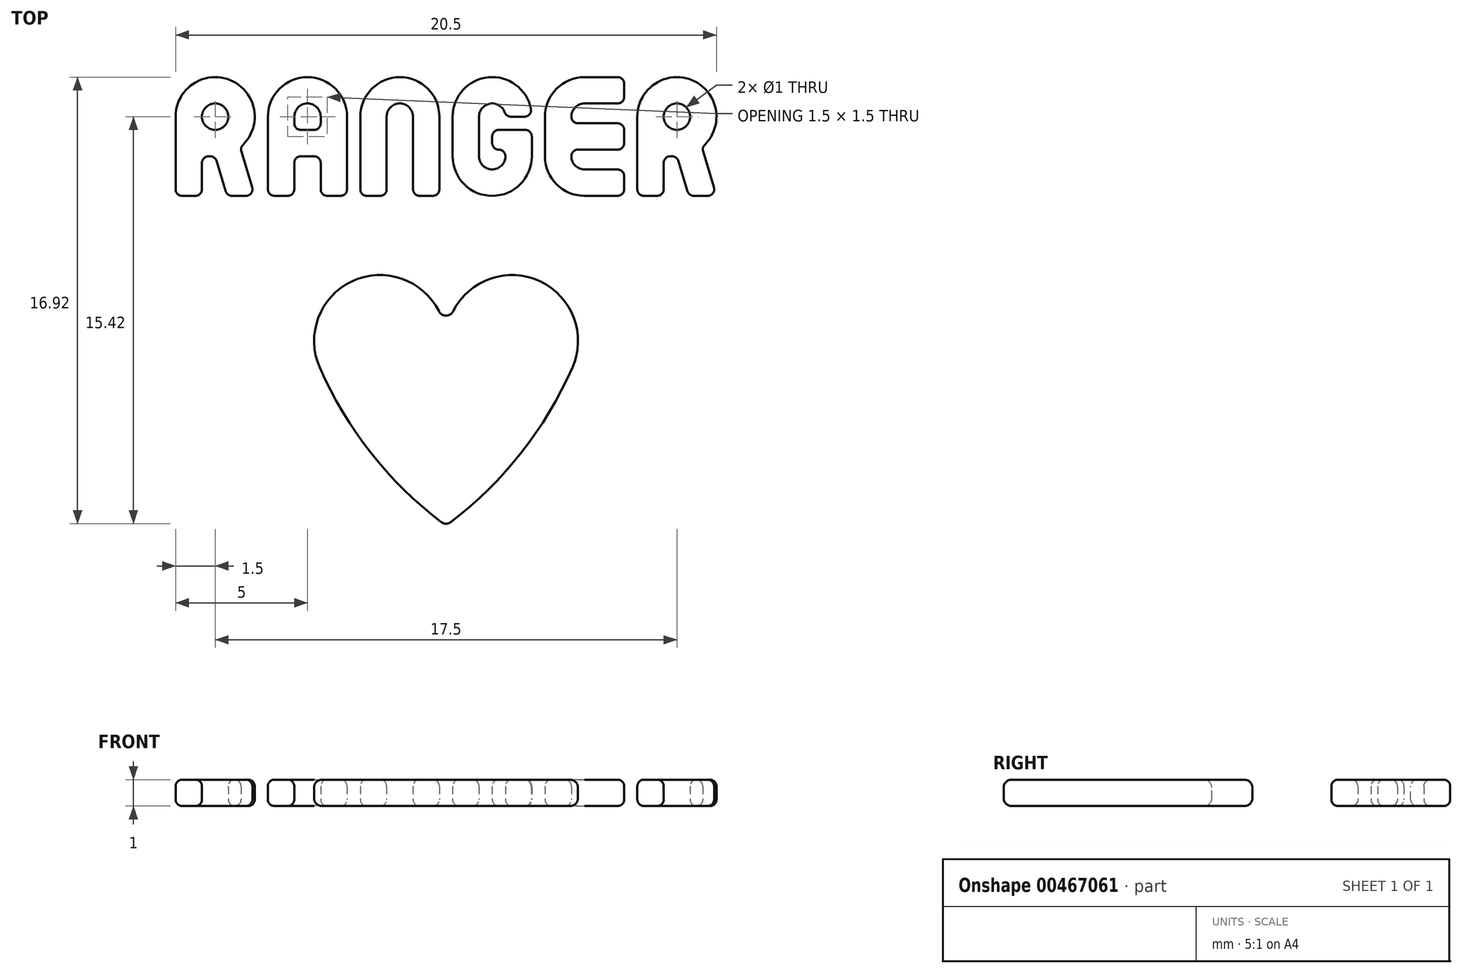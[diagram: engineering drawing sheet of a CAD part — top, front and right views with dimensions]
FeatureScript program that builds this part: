
annotation { "Feature Type Name" : "Feature", "Feature Type Description" : "" }
export const myFeature = defineFeature(function(context is Context, id is Id, definition is map)
    precondition{}
    {
        {
            var Q0;
            Q0=qCreatedBy(makeId("Top.planeOp"),FACE);
            var sketch = newSketch(context, id + "F0", { "sketchPlane" : qUnion([Q0])});
            skArc(sketch, "E0", {"start": v(-15, 3) * mm, "mid": v(-13.5, 4.5) * mm, "end": v(-12, 3) * mm});
            skLineSegment(sketch, "E1", {"start": v(-15, 3) * mm, "end": v(-15, 0) * mm});
            skLineSegment(sketch, "E2", {"start": v(-12, 3) * mm, "end": v(-12, 0) * mm});
            skLineSegment(sketch, "E3.0", {"start": v(-13, 3) * mm, "end": v(-13, 2.5) * mm});
            skArc(sketch, "E3.1", {"start": v(-14, 3) * mm, "mid": v(-13.5, 3.5) * mm, "end": v(-13, 3) * mm});
            skLineSegment(sketch, "E3.2", {"start": v(-14, 3) * mm, "end": v(-14, 2.5) * mm});
            skLineSegment(sketch, "E4.bottom", {"start": v(-14, 2.5) * mm, "end": v(-13, 2.5) * mm});
            skLineSegment(sketch, "E4.top", {"start": v(-14, 1.5) * mm, "end": v(-13, 1.5) * mm});
            skLineSegment(sketch, "E5.trimOffspring", {"start": v(-13, 1.5) * mm, "end": v(-13, 0) * mm});
            skLineSegment(sketch, "E6.trimOffspring", {"start": v(-14, 1.5) * mm, "end": v(-14, 0) * mm});
            skLineSegment(sketch, "E7", {"start": v(-15, 0) * mm, "end": v(-14, 0) * mm});
            skLineSegment(sketch, "E8.trimOffspring", {"start": v(-13, 0) * mm, "end": v(-12, 0) * mm});
            skLineSegment(sketch, "E9", {"start": v(-16.02, 4.5) * mm, "end": v(-10.39, 4.5) * mm, "construction": true});
            skArc(sketch, "E10", {"start": v(-11.5, 3) * mm, "mid": v(-10, 4.5) * mm, "end": v(-8.5, 3) * mm});
            skLineSegment(sketch, "E11", {"start": v(-11.5, 3) * mm, "end": v(-11.5, 0) * mm});
            skLineSegment(sketch, "E12", {"start": v(-8.5, 3) * mm, "end": v(-8.5, 0) * mm});
            skArc(sketch, "E13.1", {"start": v(-10.5, 3) * mm, "mid": v(-10, 3.5) * mm, "end": v(-9.5, 3) * mm});
            skLineSegment(sketch, "E13.2", {"start": v(-10.5, 3) * mm, "end": v(-10.5, 0) * mm});
            skLineSegment(sketch, "E14", {"start": v(-11.5, 0) * mm, "end": v(-10.5, 0) * mm});
            skLineSegment(sketch, "E15.trimOffspring", {"start": v(-9.5, 0) * mm, "end": v(-8.5, 0) * mm});
            skLineSegment(sketch, "E16", {"start": v(-9.5, 3) * mm, "end": v(-9.5, 0) * mm});
            skArc(sketch, "E17.0.startCap", {"start": v(-7, 3) * mm, "mid": v(-6.5, 3.5) * mm, "end": v(-6, 3) * mm});
            skArc(sketch, "E17.0.endCap", {"start": v(-6, 1.5) * mm, "mid": v(-6.5, 1) * mm, "end": v(-7, 1.5) * mm});
            skLineSegment(sketch, "E17.0.right", {"start": v(-7, 3) * mm, "end": v(-7, 1.5) * mm});
            skArc(sketch, "E18.0.startCap", {"start": v(-8, 3) * mm, "mid": v(-6.5, 4.5) * mm, "end": v(-5, 3) * mm});
            skArc(sketch, "E18.0.endCap", {"start": v(-5, 1.5) * mm, "mid": v(-6.5, 0) * mm, "end": v(-8, 1.5) * mm});
            skLineSegment(sketch, "E18.0.right", {"start": v(-8, 3) * mm, "end": v(-8, 1.5) * mm});
            skLineSegment(sketch, "E19.trimOffspring", {"start": v(-6, 1.75) * mm, "end": v(-6, 1.5) * mm});
            skLineSegment(sketch, "E20", {"start": v(-5, 1.5) * mm, "end": v(-5, 2.5) * mm});
            skLineSegment(sketch, "E21", {"start": v(-5, 2.5) * mm, "end": v(-6.5, 2.5) * mm});
            skLineSegment(sketch, "E22", {"start": v(-6.5, 2.5) * mm, "end": v(-6.5, 1.75) * mm});
            skLineSegment(sketch, "E23", {"start": v(-6.5, 1.75) * mm, "end": v(-6, 1.75) * mm});
            skLineSegment(sketch, "E24", {"start": v(-6, 3) * mm, "end": v(-5, 3) * mm});
            skArc(sketch, "E25", {"start": v(-4.5, 3) * mm, "mid": v(-4.06, 4.06) * mm, "end": v(-3, 4.5) * mm});
            skLineSegment(sketch, "E26", {"start": v(-3, 4.5) * mm, "end": v(-1.5, 4.5) * mm});
            skLineSegment(sketch, "E27", {"start": v(-1.5, 4.5) * mm, "end": v(-1.5, 3.5) * mm});
            skLineSegment(sketch, "E28", {"start": v(-1.5, 3.5) * mm, "end": v(-3, 3.5) * mm});
            skArc(sketch, "E29", {"start": v(-3, 3.5) * mm, "mid": v(-3.35, 3.35) * mm, "end": v(-3.5, 3) * mm});
            skLineSegment(sketch, "E30", {"start": v(-4.5, 3) * mm, "end": v(-4.5, 1.5) * mm});
            skLineSegment(sketch, "E31", {"start": v(-3.5, 3) * mm, "end": v(-3.5, 2.75) * mm});
            skArc(sketch, "E32", {"start": v(-3.5, 1.5) * mm, "mid": v(-3.35, 1.15) * mm, "end": v(-3, 1) * mm});
            skArc(sketch, "E33", {"start": v(-4.5, 1.5) * mm, "mid": v(-4.06, 0.44) * mm, "end": v(-3, 0) * mm});
            skLineSegment(sketch, "E34", {"start": v(-3, 1) * mm, "end": v(-1.5, 1) * mm});
            skLineSegment(sketch, "E35", {"start": v(-1.5, 1) * mm, "end": v(-1.5, 0) * mm});
            skLineSegment(sketch, "E36", {"start": v(-1.5, 0) * mm, "end": v(-3, 0) * mm});
            skLineSegment(sketch, "E37.bottom", {"start": v(-3.5, 2.75) * mm, "end": v(-1.5, 2.75) * mm});
            skLineSegment(sketch, "E37.top", {"start": v(-3.5, 1.75) * mm, "end": v(-1.5, 1.75) * mm});
            skLineSegment(sketch, "E37.right", {"start": v(-1.5, 2.75) * mm, "end": v(-1.5, 1.75) * mm});
            skLineSegment(sketch, "E38.trimOffspring", {"start": v(-3.5, 1.75) * mm, "end": v(-3.5, 1.5) * mm});
            skLineSegment(sketch, "E39", {"start": v(-1.5, 2.25) * mm, "end": v(-3.17, 2.25) * mm, "construction": true});
            skPoint(sketch, "E39.endSnap0", {"position": v(-1.5, 2.25) * mm});
            skLineSegment(sketch, "E40", {"start": v(-1, 0) * mm, "end": v(-1, 3) * mm});
            skLineSegment(sketch, "E41", {"start": v(0, 1.5) * mm, "end": v(0, 0) * mm});
            skLineSegment(sketch, "E42", {"start": v(0, 0) * mm, "end": v(-1, 0) * mm});
            skPoint(sketch, "E43.orphan", {"position": v(0, 2.75) * mm});
            skCircle(sketch, "E44", {"center": v(0.5, 3) * mm, "radius": 0.5 * mm});
            skLineSegment(sketch, "E45", {"start": v(0.5, 1.5) * mm, "end": v(0, 1.5) * mm});
            skLineSegment(sketch, "E46", {"start": v(0.5, 1.5) * mm, "end": v(0.96, 0) * mm});
            skLineSegment(sketch, "E47", {"start": v(0.96, 0) * mm, "end": v(2, 0) * mm});
            skLineSegment(sketch, "E48", {"start": v(2, 0) * mm, "end": v(1.44, 1.83) * mm});
            skArc(sketch, "E49.trimOffspring", {"start": v(1.44, 1.83) * mm, "mid": v(1.15, 4.35) * mm, "end": v(-1, 3) * mm});
            skLineSegment(sketch, "E50", {"start": v(2, 3.78) * mm, "end": v(2, 0) * mm, "construction": true});
            skLineSegment(sketch, "E51", {"start": v(0.5, 3) * mm, "end": v(0.5, 0.89) * mm, "construction": true});
            skLineSegment(sketch, "E52", {"start": v(-18.5, 0) * mm, "end": v(-18.5, 3) * mm});
            skLineSegment(sketch, "E53", {"start": v(-17.5, 1.5) * mm, "end": v(-17.5, 0) * mm});
            skLineSegment(sketch, "E54", {"start": v(-17.5, 0) * mm, "end": v(-18.5, 0) * mm});
            skCircle(sketch, "E55", {"center": v(-17, 3) * mm, "radius": 0.5 * mm});
            skLineSegment(sketch, "E56", {"start": v(-17, 1.5) * mm, "end": v(-17.5, 1.5) * mm});
            skLineSegment(sketch, "E57", {"start": v(-17, 1.5) * mm, "end": v(-16.54, 0) * mm});
            skLineSegment(sketch, "E58", {"start": v(-16.54, 0) * mm, "end": v(-15.5, 0) * mm});
            skLineSegment(sketch, "E59", {"start": v(-15.5, 0) * mm, "end": v(-16.06, 1.83) * mm});
            skArc(sketch, "E60.trimOffspring", {"start": v(-16.06, 1.83) * mm, "mid": v(-16.35, 4.35) * mm, "end": v(-18.5, 3) * mm});
            skLineSegment(sketch, "E61", {"start": v(-15.5, 5.59) * mm, "end": v(-15.5, 1.81) * mm, "construction": true});
            skLineSegment(sketch, "E62", {"start": v(-17, 3) * mm, "end": v(-17, 2.7) * mm, "construction": true});
            skSolve(sketch);
        }
        {
            var Q0;
            Q0 = qSketchRegion(id + "F0", true);
            extrude(context, id + "F1", {"entities" : qUnion([Q0]), "depth" : 1 * mm});
        }
        {
            var Q0;
            Q0=makeQuery(id+"F1.opExtrude","CAP_FACE",FACE,{"disambiguationData":[OSD([sQuery(id+"F0.wireOp",EDGE,"E52"),sQuery(id+"F0.wireOp",EDGE,"E53"),sQuery(id+"F0.wireOp",EDGE,"E54"),sQuery(id+"F0.wireOp",EDGE,"E55"),sQuery(id+"F0.wireOp",EDGE,"E56"),sQuery(id+"F0.wireOp",EDGE,"E57"),sQuery(id+"F0.wireOp",EDGE,"E58"),sQuery(id+"F0.wireOp",EDGE,"E59"),sQuery(id+"F0.wireOp",EDGE,"E60.trimOffspring")])],"isStart":false});
            var Q1;
            Q1=makeQuery(id+"F1.opExtrude","CAP_FACE",FACE,{"disambiguationData":[OSD([sQuery(id+"F0.wireOp",EDGE,"E0"),sQuery(id+"F0.wireOp",EDGE,"E1"),sQuery(id+"F0.wireOp",EDGE,"E2"),sQuery(id+"F0.wireOp",EDGE,"E3.0"),sQuery(id+"F0.wireOp",EDGE,"E3.1"),sQuery(id+"F0.wireOp",EDGE,"E3.2"),sQuery(id+"F0.wireOp",EDGE,"E4.bottom"),sQuery(id+"F0.wireOp",EDGE,"E4.top"),sQuery(id+"F0.wireOp",EDGE,"E5.trimOffspring"),sQuery(id+"F0.wireOp",EDGE,"E6.trimOffspring"),sQuery(id+"F0.wireOp",EDGE,"E7"),sQuery(id+"F0.wireOp",EDGE,"E8.trimOffspring")])],"isStart":false});
            var Q2;
            Q2=makeQuery(id+"F1.opExtrude","CAP_FACE",FACE,{"disambiguationData":[OSD([sQuery(id+"F0.wireOp",EDGE,"E10"),sQuery(id+"F0.wireOp",EDGE,"E11"),sQuery(id+"F0.wireOp",EDGE,"E12"),sQuery(id+"F0.wireOp",EDGE,"E13.1"),sQuery(id+"F0.wireOp",EDGE,"E13.2"),sQuery(id+"F0.wireOp",EDGE,"E14"),sQuery(id+"F0.wireOp",EDGE,"E15.trimOffspring"),sQuery(id+"F0.wireOp",EDGE,"E16")])],"isStart":false});
            var Q3;
            Q3=makeQuery(id+"F1.opExtrude","CAP_FACE",FACE,{"disambiguationData":[OSD([sQuery(id+"F0.wireOp",EDGE,"E17.0.startCap"),sQuery(id+"F0.wireOp",EDGE,"E17.0.endCap"),sQuery(id+"F0.wireOp",EDGE,"E17.0.right"),sQuery(id+"F0.wireOp",EDGE,"E18.0.startCap"),sQuery(id+"F0.wireOp",EDGE,"E18.0.endCap"),sQuery(id+"F0.wireOp",EDGE,"E18.0.right"),sQuery(id+"F0.wireOp",EDGE,"E19.trimOffspring"),sQuery(id+"F0.wireOp",EDGE,"E20"),sQuery(id+"F0.wireOp",EDGE,"E21"),sQuery(id+"F0.wireOp",EDGE,"E22"),sQuery(id+"F0.wireOp",EDGE,"E23"),sQuery(id+"F0.wireOp",EDGE,"E24")])],"isStart":false});
            var Q4;
            Q4=makeQuery(id+"F1.opExtrude","CAP_FACE",FACE,{"disambiguationData":[OSD([sQuery(id+"F0.wireOp",EDGE,"E25"),sQuery(id+"F0.wireOp",EDGE,"E26"),sQuery(id+"F0.wireOp",EDGE,"E27"),sQuery(id+"F0.wireOp",EDGE,"E28"),sQuery(id+"F0.wireOp",EDGE,"E29"),sQuery(id+"F0.wireOp",EDGE,"E30"),sQuery(id+"F0.wireOp",EDGE,"E31"),sQuery(id+"F0.wireOp",EDGE,"E32"),sQuery(id+"F0.wireOp",EDGE,"E33"),sQuery(id+"F0.wireOp",EDGE,"E34"),sQuery(id+"F0.wireOp",EDGE,"E35"),sQuery(id+"F0.wireOp",EDGE,"E36"),sQuery(id+"F0.wireOp",EDGE,"E37.bottom"),sQuery(id+"F0.wireOp",EDGE,"E37.top"),sQuery(id+"F0.wireOp",EDGE,"E37.right"),sQuery(id+"F0.wireOp",EDGE,"E38.trimOffspring")])],"isStart":false});
            var Q5;
            Q5=makeQuery(id+"F1.opExtrude","CAP_FACE",FACE,{"disambiguationData":[OSD([sQuery(id+"F0.wireOp",EDGE,"E40"),sQuery(id+"F0.wireOp",EDGE,"E41"),sQuery(id+"F0.wireOp",EDGE,"E42"),sQuery(id+"F0.wireOp",EDGE,"E44"),sQuery(id+"F0.wireOp",EDGE,"E45"),sQuery(id+"F0.wireOp",EDGE,"E46"),sQuery(id+"F0.wireOp",EDGE,"E47"),sQuery(id+"F0.wireOp",EDGE,"E48"),sQuery(id+"F0.wireOp",EDGE,"E49.trimOffspring")])],"isStart":false});
            var Q6;
            Q6=makeQuery(id+"F1.opExtrude","CAP_FACE",FACE,{"disambiguationData":[OSD([sQuery(id+"F0.wireOp",EDGE,"E40"),sQuery(id+"F0.wireOp",EDGE,"E41"),sQuery(id+"F0.wireOp",EDGE,"E42"),sQuery(id+"F0.wireOp",EDGE,"E44"),sQuery(id+"F0.wireOp",EDGE,"E45"),sQuery(id+"F0.wireOp",EDGE,"E46"),sQuery(id+"F0.wireOp",EDGE,"E47"),sQuery(id+"F0.wireOp",EDGE,"E48"),sQuery(id+"F0.wireOp",EDGE,"E49.trimOffspring")])],"isStart":true});
            var Q7;
            Q7=makeQuery(id+"F1.opExtrude","CAP_FACE",FACE,{"disambiguationData":[OSD([sQuery(id+"F0.wireOp",EDGE,"E25"),sQuery(id+"F0.wireOp",EDGE,"E26"),sQuery(id+"F0.wireOp",EDGE,"E27"),sQuery(id+"F0.wireOp",EDGE,"E28"),sQuery(id+"F0.wireOp",EDGE,"E29"),sQuery(id+"F0.wireOp",EDGE,"E30"),sQuery(id+"F0.wireOp",EDGE,"E31"),sQuery(id+"F0.wireOp",EDGE,"E32"),sQuery(id+"F0.wireOp",EDGE,"E33"),sQuery(id+"F0.wireOp",EDGE,"E34"),sQuery(id+"F0.wireOp",EDGE,"E35"),sQuery(id+"F0.wireOp",EDGE,"E36"),sQuery(id+"F0.wireOp",EDGE,"E37.bottom"),sQuery(id+"F0.wireOp",EDGE,"E37.top"),sQuery(id+"F0.wireOp",EDGE,"E37.right"),sQuery(id+"F0.wireOp",EDGE,"E38.trimOffspring")])],"isStart":true});
            var Q8;
            Q8=makeQuery(id+"F1.opExtrude","CAP_FACE",FACE,{"disambiguationData":[OSD([sQuery(id+"F0.wireOp",EDGE,"E17.0.startCap"),sQuery(id+"F0.wireOp",EDGE,"E17.0.endCap"),sQuery(id+"F0.wireOp",EDGE,"E17.0.right"),sQuery(id+"F0.wireOp",EDGE,"E18.0.startCap"),sQuery(id+"F0.wireOp",EDGE,"E18.0.endCap"),sQuery(id+"F0.wireOp",EDGE,"E18.0.right"),sQuery(id+"F0.wireOp",EDGE,"E19.trimOffspring"),sQuery(id+"F0.wireOp",EDGE,"E20"),sQuery(id+"F0.wireOp",EDGE,"E21"),sQuery(id+"F0.wireOp",EDGE,"E22"),sQuery(id+"F0.wireOp",EDGE,"E23"),sQuery(id+"F0.wireOp",EDGE,"E24")])],"isStart":true});
            var Q9;
            Q9=makeQuery(id+"F1.opExtrude","CAP_FACE",FACE,{"disambiguationData":[OSD([sQuery(id+"F0.wireOp",EDGE,"E10"),sQuery(id+"F0.wireOp",EDGE,"E11"),sQuery(id+"F0.wireOp",EDGE,"E12"),sQuery(id+"F0.wireOp",EDGE,"E13.1"),sQuery(id+"F0.wireOp",EDGE,"E13.2"),sQuery(id+"F0.wireOp",EDGE,"E14"),sQuery(id+"F0.wireOp",EDGE,"E15.trimOffspring"),sQuery(id+"F0.wireOp",EDGE,"E16")])],"isStart":true});
            var Q10;
            Q10=makeQuery(id+"F1.opExtrude","CAP_FACE",FACE,{"disambiguationData":[OSD([sQuery(id+"F0.wireOp",EDGE,"E0"),sQuery(id+"F0.wireOp",EDGE,"E1"),sQuery(id+"F0.wireOp",EDGE,"E2"),sQuery(id+"F0.wireOp",EDGE,"E3.0"),sQuery(id+"F0.wireOp",EDGE,"E3.1"),sQuery(id+"F0.wireOp",EDGE,"E3.2"),sQuery(id+"F0.wireOp",EDGE,"E4.bottom"),sQuery(id+"F0.wireOp",EDGE,"E4.top"),sQuery(id+"F0.wireOp",EDGE,"E5.trimOffspring"),sQuery(id+"F0.wireOp",EDGE,"E6.trimOffspring"),sQuery(id+"F0.wireOp",EDGE,"E7"),sQuery(id+"F0.wireOp",EDGE,"E8.trimOffspring")])],"isStart":true});
            var Q11;
            Q11=makeQuery(id+"F1.opExtrude","CAP_FACE",FACE,{"disambiguationData":[OSD([sQuery(id+"F0.wireOp",EDGE,"E52"),sQuery(id+"F0.wireOp",EDGE,"E53"),sQuery(id+"F0.wireOp",EDGE,"E54"),sQuery(id+"F0.wireOp",EDGE,"E55"),sQuery(id+"F0.wireOp",EDGE,"E56"),sQuery(id+"F0.wireOp",EDGE,"E57"),sQuery(id+"F0.wireOp",EDGE,"E58"),sQuery(id+"F0.wireOp",EDGE,"E59"),sQuery(id+"F0.wireOp",EDGE,"E60.trimOffspring")])],"isStart":true});
            var Q12;
            Q12=makeQuery(id+"F1.opExtrude","SWEPT_FACE",FACE,{"disambiguationData":[OSD([sQuery(id+"F0.wireOp",EDGE,"E21")])]});
            var Q13;
            Q13=makeQuery(id+"F1.opExtrude","SWEPT_FACE",FACE,{"disambiguationData":[OSD([sQuery(id+"F0.wireOp",EDGE,"E17.0.endCap")])]});
            var Q14;
            Q14=makeQuery(id+"F1.opExtrude","SWEPT_FACE",FACE,{"disambiguationData":[OSD([sQuery(id+"F0.wireOp",EDGE,"E18.0.endCap")])]});
            var Q15;
            Q15=makeQuery(id+"F1.opExtrude","SWEPT_FACE",FACE,{"disambiguationData":[OSD([sQuery(id+"F0.wireOp",EDGE,"E36")])]});
            var Q16;
            Q16=makeQuery(id+"F1.opExtrude","SWEPT_FACE",FACE,{"disambiguationData":[OSD([sQuery(id+"F0.wireOp",EDGE,"E35")])]});
            var Q17;
            Q17=makeQuery(id+"F1.opExtrude","SWEPT_FACE",FACE,{"disambiguationData":[OSD([sQuery(id+"F0.wireOp",EDGE,"E37.top")])]});
            var Q18;
            Q18=makeQuery(id+"F1.opExtrude","SWEPT_FACE",FACE,{"disambiguationData":[OSD([sQuery(id+"F0.wireOp",EDGE,"E34")])]});
            var Q19;
            Q19=makeQuery(id+"F1.opExtrude","SWEPT_FACE",FACE,{"disambiguationData":[OSD([sQuery(id+"F0.wireOp",EDGE,"E37.bottom")])]});
            var Q20;
            Q20=makeQuery(id+"F1.opExtrude","SWEPT_FACE",FACE,{"disambiguationData":[OSD([sQuery(id+"F0.wireOp",EDGE,"E28")])]});
            var Q21;
            Q21=makeQuery(id+"F1.opExtrude","SWEPT_FACE",FACE,{"disambiguationData":[OSD([sQuery(id+"F0.wireOp",EDGE,"E26")])]});
            var Q22;
            Q22=makeQuery(id+"F1.opExtrude","SWEPT_FACE",FACE,{"disambiguationData":[OSD([sQuery(id+"F0.wireOp",EDGE,"E47")])]});
            var Q23;
            Q23=makeQuery(id+"F1.opExtrude","SWEPT_FACE",FACE,{"disambiguationData":[OSD([sQuery(id+"F0.wireOp",EDGE,"E42")])]});
            var Q24;
            Q24=makeQuery(id+"F1.opExtrude","SWEPT_FACE",FACE,{"disambiguationData":[OSD([sQuery(id+"F0.wireOp",EDGE,"E45")])]});
            var Q25;
            Q25=makeQuery(id+"F1.opExtrude","SWEPT_FACE",FACE,{"disambiguationData":[OSD([sQuery(id+"F0.wireOp",EDGE,"E41")])]});
            var Q26;
            Q26=makeQuery(id+"F1.opExtrude","SWEPT_FACE",FACE,{"disambiguationData":[OSD([sQuery(id+"F0.wireOp",EDGE,"E46")])]});
            var Q27;
            Q27=makeQuery(id+"F1.opExtrude","SWEPT_FACE",FACE,{"disambiguationData":[OSD([sQuery(id+"F0.wireOp",EDGE,"E49.trimOffspring")])]});
            var Q28;
            Q28=makeQuery(id+"F1.opExtrude","SWEPT_FACE",FACE,{"disambiguationData":[OSD([sQuery(id+"F0.wireOp",EDGE,"E23")])]});
            var Q29;
            Q29=makeQuery(id+"F1.opExtrude","SWEPT_FACE",FACE,{"disambiguationData":[OSD([sQuery(id+"F0.wireOp",EDGE,"E24")])]});
            var Q30;
            Q30=makeQuery(id+"F1.opExtrude","SWEPT_FACE",FACE,{"disambiguationData":[OSD([sQuery(id+"F0.wireOp",EDGE,"E17.0.startCap")])]});
            var Q31;
            Q31=makeQuery(id+"F1.opExtrude","SWEPT_FACE",FACE,{"disambiguationData":[OSD([sQuery(id+"F0.wireOp",EDGE,"E15.trimOffspring")])]});
            var Q32;
            Q32=makeQuery(id+"F1.opExtrude","SWEPT_FACE",FACE,{"disambiguationData":[OSD([sQuery(id+"F0.wireOp",EDGE,"E14")])]});
            var Q33;
            Q33=makeQuery(id+"F1.opExtrude","SWEPT_FACE",FACE,{"disambiguationData":[OSD([sQuery(id+"F0.wireOp",EDGE,"E8.trimOffspring")])]});
            var Q34;
            Q34=makeQuery(id+"F1.opExtrude","SWEPT_FACE",FACE,{"disambiguationData":[OSD([sQuery(id+"F0.wireOp",EDGE,"E4.bottom")])]});
            var Q35;
            Q35=makeQuery(id+"F1.opExtrude","SWEPT_FACE",FACE,{"disambiguationData":[OSD([sQuery(id+"F0.wireOp",EDGE,"E4.top")])]});
            var Q36;
            Q36=makeQuery(id+"F1.opExtrude","SWEPT_FACE",FACE,{"disambiguationData":[OSD([sQuery(id+"F0.wireOp",EDGE,"E7")])]});
            var Q37;
            Q37=makeQuery(id+"F1.opExtrude","SWEPT_FACE",FACE,{"disambiguationData":[OSD([sQuery(id+"F0.wireOp",EDGE,"E58")])]});
            var Q38;
            Q38=makeQuery(id+"F1.opExtrude","SWEPT_FACE",FACE,{"disambiguationData":[OSD([sQuery(id+"F0.wireOp",EDGE,"E54")])]});
            var Q39;
            Q39=makeQuery(id+"F1.opExtrude","SWEPT_FACE",FACE,{"disambiguationData":[OSD([sQuery(id+"F0.wireOp",EDGE,"E56")])]});
            var Q40;
            Q40=makeQuery(id+"F1.opExtrude","SWEPT_FACE",FACE,{"disambiguationData":[OSD([sQuery(id+"F0.wireOp",EDGE,"E53")])]});
            var Q41;
            Q41=makeQuery(id+"F1.opExtrude","SWEPT_FACE",FACE,{"disambiguationData":[OSD([sQuery(id+"F0.wireOp",EDGE,"E57")])]});
            var Q42;
            Q42=makeQuery(id+"F1.opExtrude","SWEPT_FACE",FACE,{"disambiguationData":[OSD([sQuery(id+"F0.wireOp",EDGE,"E59")])]});
            fillet(context, id + "F2", {"entities" : qUnion([Q0, Q1, Q2, Q3, Q4, Q5, Q6, Q7, Q8, Q9, Q10, Q11, Q12, Q13, Q14, Q15, Q16, Q17, Q18, Q19, Q20, Q21, Q22, Q23, Q24, Q25, Q26, Q27, Q28, Q29, Q30, Q31, Q32, Q33, Q34, Q35, Q36, Q37, Q38, Q39, Q40, Q41, Q42]), "radius" : 0.25 * mm, "tangentPropagation" : true, "allowEdgeOverflow" : false});
        }
        {
            var Q0;
            Q0=qCreatedBy(makeId("Top.planeOp"),FACE);
            var sketch = newSketch(context, id + "F3", { "sketchPlane" : qUnion([Q0])});
            skLineSegment(sketch, "E63", {"start": v(-18.5, 7.97) * mm, "end": v(-18.5, -3.28) * mm, "construction": true});
            skLineSegment(sketch, "E64", {"start": v(2, 6.07) * mm, "end": v(2, -1.75) * mm, "construction": true});
            skLineSegment(sketch, "E65", {"start": v(-8.25, 12.89) * mm, "end": v(-8.25, -5.5) * mm, "construction": true});
            skArc(sketch, "E66", {"start": v(-8.25, -5.5) * mm, "mid": v(-11.27, -3.05) * mm, "end": v(-13.04, -6.5) * mm});
            skArc(sketch, "E67.MirrorC", {"start": v(-8.25, -5.5) * mm, "mid": v(-5.23, -3.05) * mm, "end": v(-3.46, -6.5) * mm});
            skArc(sketch, "E68", {"start": v(-13.04, -6.5) * mm, "mid": v(-11.03, -9.82) * mm, "end": v(-8.25, -12.5) * mm});
            skArc(sketch, "E69.MirrorCS", {"start": v(-3.46, -6.5) * mm, "mid": v(-5.47, -9.82) * mm, "end": v(-8.25, -12.5) * mm});
            skLineSegment(sketch, "E70", {"start": v(-10.75, -5.5) * mm, "end": v(-5.75, -5.5) * mm, "construction": true});
            skSolve(sketch);
        }
        {
            var Q0;
            Q0=makeQuery(id+"F3.imprint","IMPRINT",FACE,{"disambiguationData":[TD([[makeQuery(id+"F3.imprint","IMPRINT",EDGE,{"derivedFrom":sQuery(id+"F3.wireOp",EDGE,"E66")}),1.0]])]});
            extrude(context, id + "F4", {"entities" : qUnion([Q0]), "depth" : 1 * mm});
        }
        {
            var Q0;
            Q0=makeQuery(id+"F4.opExtrude","SWEPT_FACE",FACE,{"disambiguationData":[OSD([sQuery(id+"F3.wireOp",EDGE,"E66")])]});
            var Q1;
            Q1=makeQuery(id+"F4.opExtrude","SWEPT_FACE",FACE,{"disambiguationData":[OSD([sQuery(id+"F3.wireOp",EDGE,"E67.MirrorC")])]});
            var Q2;
            Q2=makeQuery(id+"F4.opExtrude","SWEPT_EDGE",EDGE,{"disambiguationData":[OSD([sQuery(id+"F3.wireOp",EDGE,"E68"),sQuery(id+"F3.wireOp",EDGE,"E69.MirrorCS")])]});
            fillet(context, id + "F5", {"entities" : qUnion([Q0, Q1, Q2]), "radius" : 0.3 * mm, "tangentPropagation" : true, "allowEdgeOverflow" : false});
        }
    });
